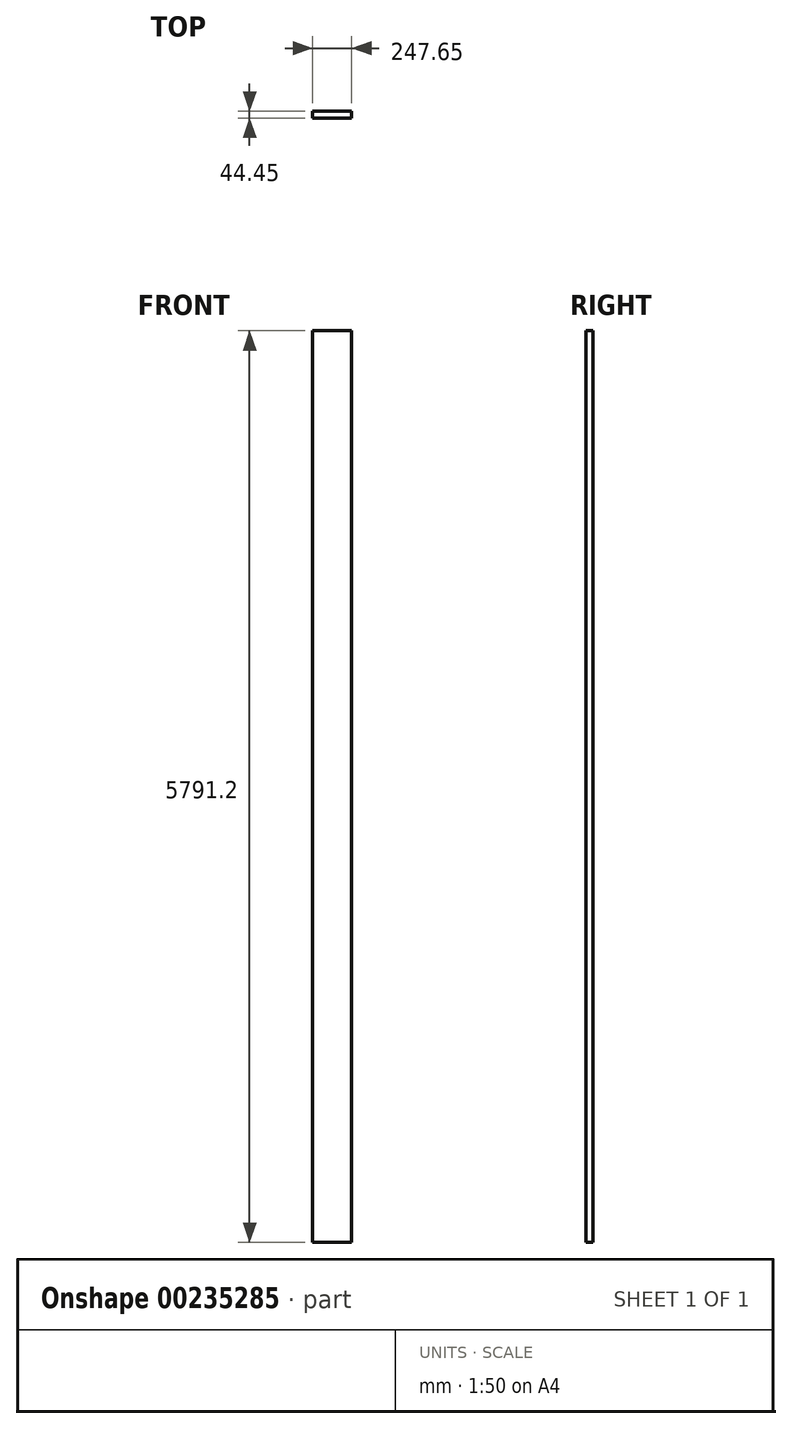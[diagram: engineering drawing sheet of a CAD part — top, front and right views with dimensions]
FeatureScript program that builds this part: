
annotation { "Feature Type Name" : "Feature", "Feature Type Description" : "" }
export const myFeature = defineFeature(function(context is Context, id is Id, definition is map)
    precondition{}
    {
        {
            var Q0;
            Q0=qCreatedBy(makeId("Top.planeOp"),FACE);
            var sketch = newSketch(context, id + "F0", { "sketchPlane" : qUnion([Q0])});
            skLineSegment(sketch, "E0", {"start": v(0, 0) * mm, "end": v(0, 44.45) * mm});
            skLineSegment(sketch, "E1", {"start": v(0, 0) * mm, "end": v(247.65, 0) * mm});
            skLineSegment(sketch, "E2", {"start": v(247.65, 0) * mm, "end": v(247.65, 44.45) * mm});
            skLineSegment(sketch, "E3", {"start": v(247.65, 44.45) * mm, "end": v(0, 44.45) * mm});
            skSolve(sketch);
        }
        {
            var Q0;
            Q0=makeQuery(id+"F0.imprint","IMPRINT",FACE,{"disambiguationData":[TD([[makeQuery(id+"F0.imprint","IMPRINT",EDGE,{"derivedFrom":sQuery(id+"F0.wireOp",EDGE,"E0")}),-1.0]])]});
            extrude(context, id + "F1", {"entities" : qUnion([Q0]), "offsetDistance" : 25.4 * mm, "depth" : 5791.2 * mm});
        }
    });
